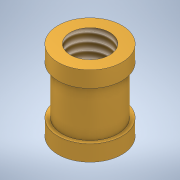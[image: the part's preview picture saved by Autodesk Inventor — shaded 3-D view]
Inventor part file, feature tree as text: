
AUTODESK INVENTOR PART (.ipt)
format: ipt  version: 2020 (Build 240168000, 168)  size: 133,632 bytes
history: native  units: in
note: dims shown in document units (in); Inventor stores cm internally (conversion verified against a paired STEP export)
features: sketch x2, revolve x1, hole x1
ambient origin geometry x8: Origin, YZ Plane, XZ Plane, XY Plane, X Axis, Y Axis, Z Axis, Center Point
bodies: Solid1 (feature_tree)
feature tree (4):
  revolve  "Revolution1"  Angle=90.0deg
  hole  "Hole1"  [1 undecoded]
  sketch  "Sketch1"  dims[d0=0.0787in d1=90.0deg]
  sketch  "Sketch2"  dims[d2=0.0394in d3=0.0098in d4=0.1181in d5=90.0deg d6=0.0098in d7=0.0394in d8=90.0deg d9=0.0787in d10=90.0deg d11=90.0deg d12=0.0968in d13=0.2362in d14=0.1575in d15=0.0787in d16=90.0deg d17=0.3465in d18=0.8108in]
note: 1 required parameter value undecoded (feature->parameter linkage not recoverable at this tier; creation-order binding heuristic only, values carry confidence <= 0.55)
